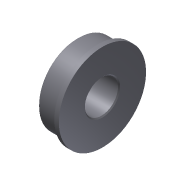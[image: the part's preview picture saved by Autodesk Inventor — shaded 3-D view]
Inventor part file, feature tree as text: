
AUTODESK INVENTOR PART (.ipt)
format: ipt  version: 2011 (Build 150239000, 239)  size: 101,376 bytes
history: native  units: in
note: dims shown in document units (in); Inventor stores cm internally (conversion verified against a paired STEP export)
features: chamfer x1, imported_body x1
ambient origin geometry x8: Origin, YZ Plane, XZ Plane, XY Plane, X Axis, Y Axis, Z Axis, Center Point
feature tree (2):
  chamfer  "Chamfer1"  [1 undecoded]
  imported_body  "Base1"
note: 1 required parameter value undecoded (feature->parameter linkage not recoverable at this tier; creation-order binding heuristic only, values carry confidence <= 0.55)
